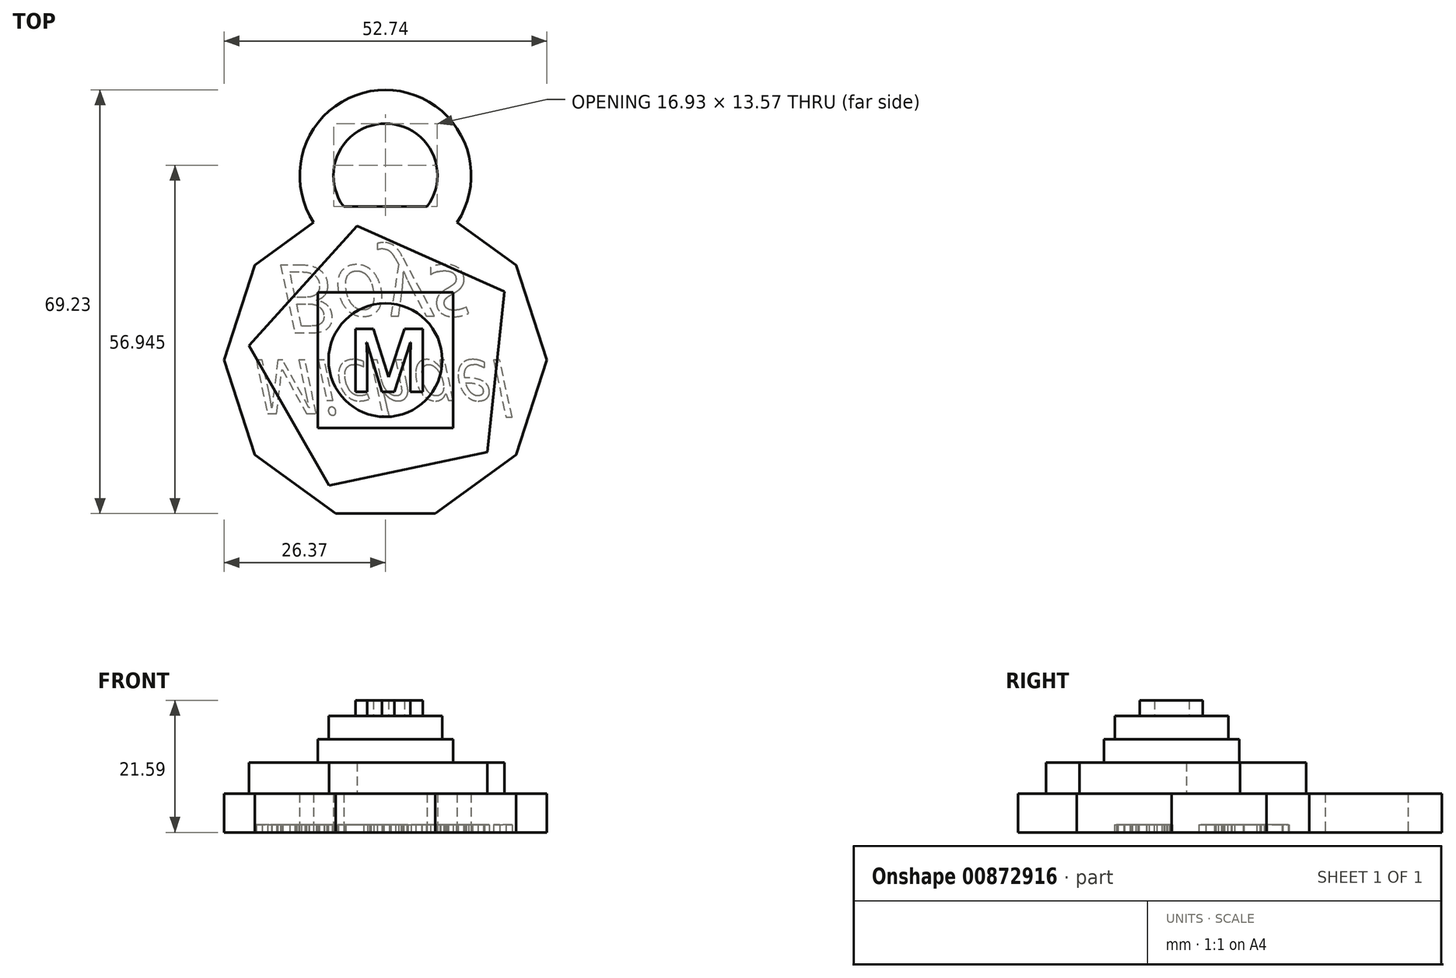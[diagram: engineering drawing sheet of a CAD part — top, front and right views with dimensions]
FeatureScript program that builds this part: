
annotation { "Feature Type Name" : "Feature", "Feature Type Description" : "" }
export const myFeature = defineFeature(function(context is Context, id is Id, definition is map)
    precondition{}
    {
        {
            var Q0;
            Q0=qCreatedBy(makeId("Top.planeOp"),FACE);
            var sketch = newSketch(context, id + "F0", { "sketchPlane" : qUnion([Q0])});
            skCircle(sketch, "E0.cCircle", {"center": v(0, 0) * mm, "radius": 25.08 * mm, "construction": true});
            skLineSegment(sketch, "E0.0", {"start": v(8.15, -25.08) * mm, "end": v(-8.15, -25.08) * mm});
            skLineSegment(sketch, "E0.1", {"start": v(-8.15, -25.08) * mm, "end": v(-21.33, -15.5) * mm});
            skLineSegment(sketch, "E0.2", {"start": v(-21.33, -15.5) * mm, "end": v(-26.37, 0) * mm});
            skLineSegment(sketch, "E0.3", {"start": v(-26.37, 0) * mm, "end": v(-21.33, 15.5) * mm});
            skLineSegment(sketch, "E0.4", {"start": v(-21.33, 15.5) * mm, "end": v(-8.15, 25.08) * mm});
            skLineSegment(sketch, "E0.5", {"start": v(-8.15, 25.08) * mm, "end": v(8.15, 25.08) * mm});
            skLineSegment(sketch, "E0.6", {"start": v(8.15, 25.08) * mm, "end": v(21.33, 15.5) * mm});
            skLineSegment(sketch, "E0.7", {"start": v(21.33, 15.5) * mm, "end": v(26.37, 0) * mm});
            skLineSegment(sketch, "E0.8", {"start": v(26.37, 0) * mm, "end": v(21.33, -15.5) * mm});
            skLineSegment(sketch, "E0.9", {"start": v(21.33, -15.5) * mm, "end": v(8.15, -25.08) * mm});
            skPoint(sketch, "E0.0.midPoint", {"position": v(0, -25.08) * mm});
            skSolve(sketch);
        }
        {
            var Q0;
            Q0=makeQuery(id+"F0.imprint","IMPRINT",FACE,{"disambiguationData":[TD([[makeQuery(id+"F0.imprint","IMPRINT",EDGE,{"derivedFrom":sQuery(id+"F0.wireOp",EDGE,"E0.0")}),-1.0]])]});
            extrude(context, id + "F1", {"entities" : qUnion([Q0]), "depth" : 6.35 * mm, "offsetDistance" : 25.4 * mm});
        }
        {
            var Q0;
            Q0=makeQuery(id+"F1.opExtrude","CAP_FACE",FACE,{"disambiguationData":[OSD([sQuery(id+"F0.wireOp",EDGE,"E0.0"),sQuery(id+"F0.wireOp",EDGE,"E0.1"),sQuery(id+"F0.wireOp",EDGE,"E0.2"),sQuery(id+"F0.wireOp",EDGE,"E0.3"),sQuery(id+"F0.wireOp",EDGE,"E0.4"),sQuery(id+"F0.wireOp",EDGE,"E0.5"),sQuery(id+"F0.wireOp",EDGE,"E0.6"),sQuery(id+"F0.wireOp",EDGE,"E0.7"),sQuery(id+"F0.wireOp",EDGE,"E0.8"),sQuery(id+"F0.wireOp",EDGE,"E0.9")])],"isStart":false});
            var sketch = newSketch(context, id + "F2", { "sketchPlane" : qUnion([Q0])});
            skCircle(sketch, "E1.cCircle", {"center": v(0, 0) * mm, "radius": 18.15 * mm, "construction": true});
            skLineSegment(sketch, "E1.0", {"start": v(-9.17, -20.47) * mm, "end": v(-22.3, 2.4) * mm});
            skLineSegment(sketch, "E1.1", {"start": v(-22.3, 2.4) * mm, "end": v(-4.61, 21.95) * mm});
            skLineSegment(sketch, "E1.2", {"start": v(-4.61, 21.95) * mm, "end": v(19.45, 11.17) * mm});
            skLineSegment(sketch, "E1.3", {"start": v(19.45, 11.17) * mm, "end": v(16.63, -15.05) * mm});
            skLineSegment(sketch, "E1.4", {"start": v(16.63, -15.05) * mm, "end": v(-9.17, -20.47) * mm});
            skPoint(sketch, "E1.0.midPoint", {"position": v(-15.74, -9.04) * mm});
            skSolve(sketch);
        }
        {
            var Q0;
            Q0=makeQuery(id+"F2.imprint","IMPRINT",FACE,{"disambiguationData":[TD([[makeQuery(id+"F2.imprint","IMPRINT",EDGE,{"derivedFrom":sQuery(id+"F2.wireOp",EDGE,"E1.0")}),-1.0]])]});
            extrude(context, id + "F3", {"entities" : qUnion([Q0]), "operationType" : NewBodyOperationType.ADD, "depth" : 5.08 * mm, "offsetDistance" : 25.4 * mm});
        }
        {
            var Q0;
            Q0=makeQuery(id+"F3.opExtrude","CAP_FACE",FACE,{"disambiguationData":[OSD([sQuery(id+"F2.wireOp",EDGE,"E1.0"),sQuery(id+"F2.wireOp",EDGE,"E1.1"),sQuery(id+"F2.wireOp",EDGE,"E1.2"),sQuery(id+"F2.wireOp",EDGE,"E1.3"),sQuery(id+"F2.wireOp",EDGE,"E1.4")])],"isStart":false});
            var sketch = newSketch(context, id + "F4", { "sketchPlane" : qUnion([Q0])});
            skCircle(sketch, "E2.cCircle", {"center": v(0, 0) * mm, "radius": 11.07 * mm, "construction": true});
            skLineSegment(sketch, "E2.0", {"start": v(11.07, 11.07) * mm, "end": v(11.07, -11.07) * mm});
            skLineSegment(sketch, "E2.1", {"start": v(11.07, -11.07) * mm, "end": v(-11.07, -11.07) * mm});
            skLineSegment(sketch, "E2.2", {"start": v(-11.07, -11.07) * mm, "end": v(-11.07, 11.07) * mm});
            skLineSegment(sketch, "E2.3", {"start": v(-11.07, 11.07) * mm, "end": v(11.07, 11.07) * mm});
            skPoint(sketch, "E2.0.midPoint", {"position": v(11.07, 0) * mm});
            skSolve(sketch);
        }
        {
            var Q0;
            Q0=makeQuery(id+"F4.imprint","IMPRINT",FACE,{"disambiguationData":[TD([[makeQuery(id+"F4.imprint","IMPRINT",EDGE,{"derivedFrom":sQuery(id+"F4.wireOp",EDGE,"E2.0")}),-1.0]])]});
            extrude(context, id + "F5", {"entities" : qUnion([Q0]), "operationType" : NewBodyOperationType.ADD, "depth" : 3.8 * mm, "offsetDistance" : 25.4 * mm});
        }
        {
            var Q0;
            Q0=makeQuery(id+"F5.opExtrude","CAP_FACE",FACE,{"disambiguationData":[OSD([sQuery(id+"F4.wireOp",EDGE,"E2.0"),sQuery(id+"F4.wireOp",EDGE,"E2.1"),sQuery(id+"F4.wireOp",EDGE,"E2.2"),sQuery(id+"F4.wireOp",EDGE,"E2.3")])],"isStart":false});
            var sketch = newSketch(context, id + "F6", { "sketchPlane" : qUnion([Q0])});
            skCircle(sketch, "E3", {"center": v(0, 0) * mm, "radius": 9.28 * mm});
            skSolve(sketch);
        }
        {
            var Q0;
            Q0=makeQuery(id+"F6.imprint","IMPRINT",FACE,{"disambiguationData":[TD([[makeQuery(id+"F6.imprint","IMPRINT",EDGE,{"derivedFrom":sQuery(id+"F6.wireOp",EDGE,"E3")}),1.0]])]});
            extrude(context, id + "F7", {"entities" : qUnion([Q0]), "operationType" : NewBodyOperationType.ADD, "depth" : 3.8 * mm, "offsetDistance" : 25.4 * mm});
        }
        {
            var Q0;
            Q0=makeQuery(id+"F7.opExtrude","CAP_FACE",FACE,{"disambiguationData":[OSD([sQuery(id+"F6.wireOp",EDGE,"E3")])],"isStart":false});
            var sketch = newSketch(context, id + "F8", { "sketchPlane" : qUnion([Q0])});
            skText(sketch, "E4", { "text": "M", "fontName": "OpenSans-Bold.ttf"});
            const initialGuessF8  = {"E4": [-0.0062, -0.00518, 1, 0, 0.01036]};
            skSetInitialGuess(sketch, initialGuessF8);
            skSolve(sketch);
        }
        {
            var Q0;
            Q0 = qSketchRegion(id + "F8", true);
            extrude(context, id + "F9", {"entities" : qUnion([Q0]), "operationType" : NewBodyOperationType.ADD, "depth" : 2.54 * mm, "offsetDistance" : 25.4 * mm});
        }
        {
            var Q0;
            Q0=qCreatedBy(makeId("Top.planeOp"),FACE);
            var sketch = newSketch(context, id + "F10", { "sketchPlane" : qUnion([Q0])});
            skCircle(sketch, "E5", {"center": v(0, 30.16) * mm, "radius": 8.5 * mm});
            skCircle(sketch, "E6", {"center": v(0, 30.16) * mm, "radius": 14 * mm});
            skSolve(sketch);
        }
        {
            var Q0;
            Q0=makeQuery(id+"F10.imprint","IMPRINT",FACE,{"disambiguationData":[TD([[makeQuery(id+"F10.imprint","IMPRINT",EDGE,{"derivedFrom":sQuery(id+"F10.wireOp",EDGE,"E5")}),-1.0]])]});
            extrude(context, id + "F11", {"entities" : qUnion([Q0]), "operationType" : NewBodyOperationType.ADD, "depth" : 6.35 * mm, "offsetDistance" : 25.4 * mm});
        }
        {
            var Q0;
            Q0=makeQuery(id+"F11.boolean.opBoolean","MERGE",FACE,{"derivedFrom":[makeQuery(id+"F1.opExtrude","CAP_FACE",FACE,{"disambiguationData":[OSD([sQuery(id+"F0.wireOp",EDGE,"E0.0"),sQuery(id+"F0.wireOp",EDGE,"E0.1"),sQuery(id+"F0.wireOp",EDGE,"E0.2"),sQuery(id+"F0.wireOp",EDGE,"E0.3"),sQuery(id+"F0.wireOp",EDGE,"E0.4"),sQuery(id+"F0.wireOp",EDGE,"E0.5"),sQuery(id+"F0.wireOp",EDGE,"E0.6"),sQuery(id+"F0.wireOp",EDGE,"E0.7"),sQuery(id+"F0.wireOp",EDGE,"E0.8"),sQuery(id+"F0.wireOp",EDGE,"E0.9")])],"isStart":true}),makeQuery(id+"F11.opExtrude","CAP_FACE",FACE,{"disambiguationData":[OSD([sQuery(id+"F10.wireOp",EDGE,"E5"),sQuery(id+"F10.wireOp",EDGE,"E6")])],"isStart":true})]});
            var sketch = newSketch(context, id + "F12", { "sketchPlane" : qUnion([Q0])});
            skText(sketch, "E7", { "text": "Michael", "fontName": "OpenSans-Italic.ttf"});
            const initialGuessF12  = {"E7": [-0.02161, 0, 1, 0, 0.00883]};
            skSetInitialGuess(sketch, initialGuessF12);
            skSolve(sketch);
        }
        {
            var Q0;
            Q0 = qSketchRegion(id + "F12", true);
            extrude(context, id + "F13", {"entities" : qUnion([Q0]), "operationType" : NewBodyOperationType.REMOVE, "oppositeDirection" : true, "depth" : 1.27 * mm, "offsetDistance" : 25.4 * mm});
        }
        {
            var Q0;
            {var subQ0=sQuery(id+"F10.wireOp",EDGE,"E6");var subQ1=sQuery(id+"F0.wireOp",EDGE,"E0.6");var subQ2=sQuery(id+"F0.wireOp",EDGE,"E0.2");var subQ3=sQuery(id+"F0.wireOp",EDGE,"E0.9");var subQ4=sQuery(id+"F0.wireOp",EDGE,"E0.1");var subQ5=sQuery(id+"F0.wireOp",EDGE,"E0.3");var subQ6=sQuery(id+"F10.wireOp",EDGE,"E5");var subQ7=sQuery(id+"F0.wireOp",EDGE,"E0.0");var subQ8=sQuery(id+"F0.wireOp",EDGE,"E0.4");var subQ9=sQuery(id+"F0.wireOp",EDGE,"E0.5");var subQ10=sQuery(id+"F0.wireOp",EDGE,"E0.7");var subQ11=sQuery(id+"F0.wireOp",EDGE,"E0.8");Q0=makeQuery(id+"F13.boolean.opBoolean","SPLIT",FACE,{"disambiguationData":[TD([makeQuery(id+"F1.opExtrude","SWEPT_FACE",FACE,{"disambiguationData":[OSD([subQ7])]})])],"derivedFrom":makeQuery(id+"F11.boolean.opBoolean","MERGE",FACE,{"derivedFrom":[makeQuery(id+"F1.opExtrude","CAP_FACE",FACE,{"disambiguationData":[OSD([subQ7,subQ4,subQ2,subQ5,subQ8,subQ9,subQ1,subQ10,subQ11,subQ3])],"isStart":true}),makeQuery(id+"F11.opExtrude","CAP_FACE",FACE,{"disambiguationData":[OSD([subQ6,subQ0])],"isStart":true})]})});}
            var sketch = newSketch(context, id + "F14", { "sketchPlane" : qUnion([Q0])});
            skText(sketch, "E8", { "text": "Boys", "fontName": "OpenSans-Italic.ttf"});
            const initialGuessF14  = {"E8": [-0.01777, -0.0155, 1, 0, 0.01113]};
            skSetInitialGuess(sketch, initialGuessF14);
            skSolve(sketch);
        }
        {
            var Q0;
            Q0 = qSketchRegion(id + "F14", true);
            extrude(context, id + "F15", {"entities" : qUnion([Q0]), "operationType" : NewBodyOperationType.REMOVE, "oppositeDirection" : true, "depth" : 1.27 * mm, "offsetDistance" : 25.4 * mm});
        }
    });
